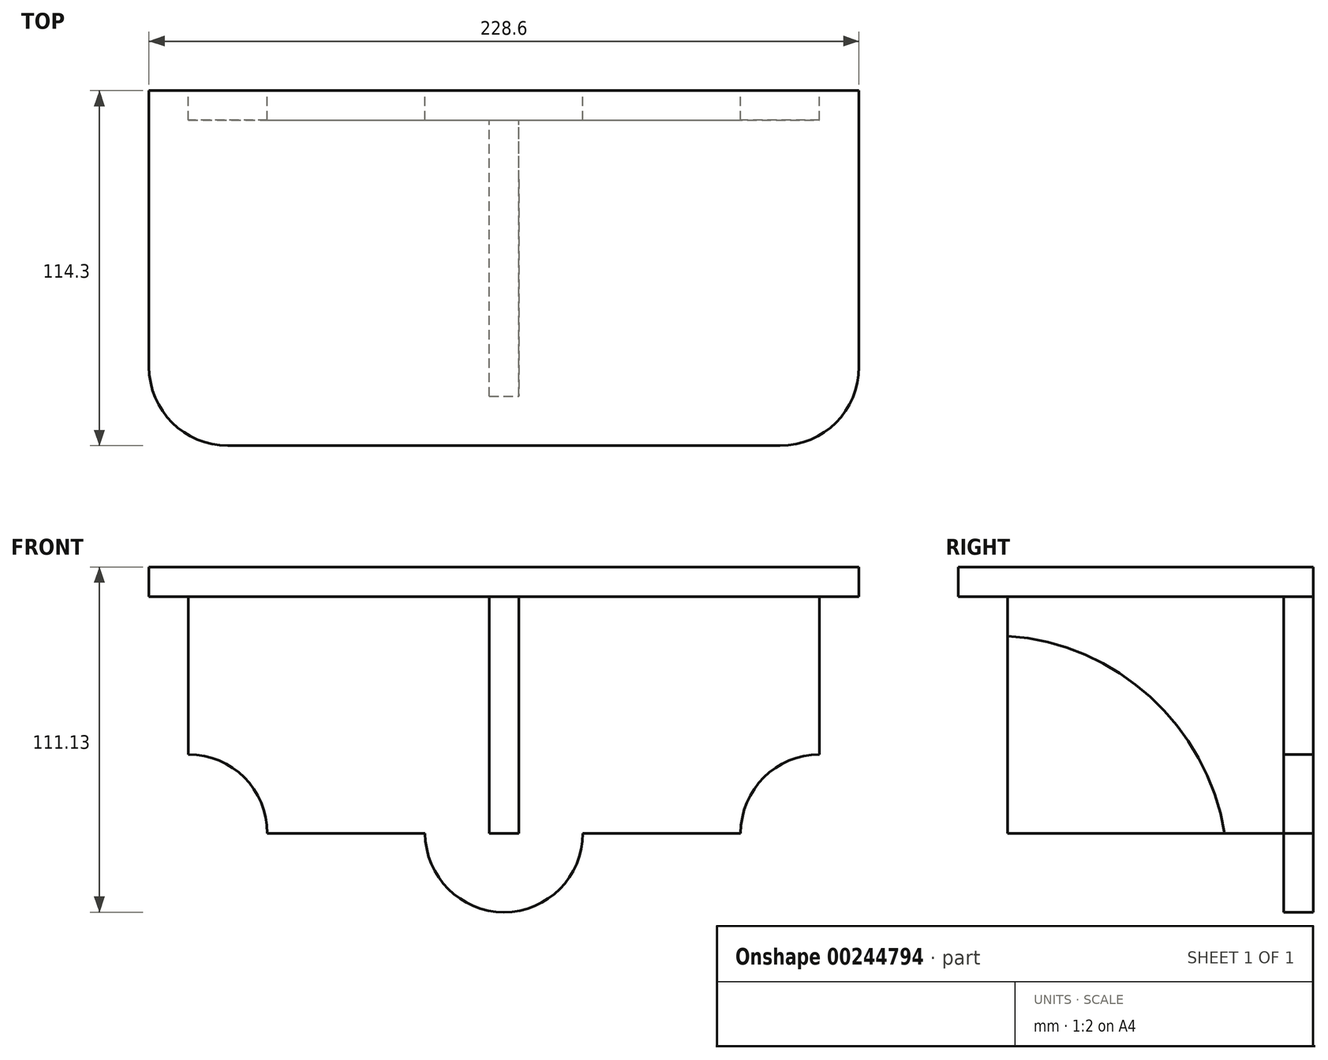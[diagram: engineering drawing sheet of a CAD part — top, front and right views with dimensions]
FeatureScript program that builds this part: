
annotation { "Feature Type Name" : "Feature", "Feature Type Description" : "" }
export const myFeature = defineFeature(function(context is Context, id is Id, definition is map)
    precondition{}
    {
        {
            var Q0;
            Q0=qCreatedBy(makeId("Front.planeOp"),FACE);
            var sketch = newSketch(context, id + "F0", { "sketchPlane" : qUnion([Q0])});
            skLineSegment(sketch, "E0", {"start": v(0, 0) * mm, "end": v(203.2, 0) * mm});
            skLineSegment(sketch, "E1", {"start": v(0, 0) * mm, "end": v(0, -50.8) * mm});
            skLineSegment(sketch, "E2", {"start": v(25.4, -76.2) * mm, "end": v(76.2, -76.2) * mm});
            skArc(sketch, "E3", {"start": v(0, -50.8) * mm, "mid": v(17.96, -58.24) * mm, "end": v(25.4, -76.2) * mm});
            skLineSegment(sketch, "E4", {"start": v(127, -76.2) * mm, "end": v(177.8, -76.2) * mm});
            skLineSegment(sketch, "E5", {"start": v(203.2, -50.8) * mm, "end": v(203.2, 0) * mm});
            skArc(sketch, "E6", {"start": v(127, -76.2) * mm, "mid": v(101.6, -101.6) * mm, "end": v(76.2, -76.2) * mm});
            skArc(sketch, "E7", {"start": v(203.2, -50.8) * mm, "mid": v(185.24, -58.24) * mm, "end": v(177.8, -76.2) * mm});
            skSolve(sketch);
        }
        {
            var Q0;
            Q0=makeQuery(id+"F0.imprint","IMPRINT",FACE,{"disambiguationData":[TD([[makeQuery(id+"F0.imprint","IMPRINT",EDGE,{"derivedFrom":sQuery(id+"F0.wireOp",EDGE,"E0")}),-1.0]])]});
            extrude(context, id + "F1", {"entities" : qUnion([Q0]), "depth" : 9.52 * mm});
        }
        {
            var Q0;
            Q0=makeQuery(id+"F1.opExtrude","CAP_FACE",FACE,{"disambiguationData":[OSD([sQuery(id+"F0.wireOp",EDGE,"E0"),sQuery(id+"F0.wireOp",EDGE,"E1"),sQuery(id+"F0.wireOp",EDGE,"E2"),sQuery(id+"F0.wireOp",EDGE,"E3"),sQuery(id+"F0.wireOp",EDGE,"E4"),sQuery(id+"F0.wireOp",EDGE,"E5"),sQuery(id+"F0.wireOp",EDGE,"E6"),sQuery(id+"F0.wireOp",EDGE,"E7")])],"isStart":false});
            var sketch = newSketch(context, id + "F2", { "sketchPlane" : qUnion([Q0])});
            skLineSegment(sketch, "E8", {"start": v(96.84, -76.2) * mm, "end": v(106.36, -76.2) * mm});
            skLineSegment(sketch, "E9", {"start": v(101.6, -76.2) * mm, "end": v(106.36, -76.2) * mm});
            skLineSegment(sketch, "E10", {"start": v(106.36, -76.2) * mm, "end": v(96.84, -76.2) * mm});
            skLineSegment(sketch, "E11", {"start": v(106.36, -76.2) * mm, "end": v(106.36, 0) * mm});
            skLineSegment(sketch, "E12", {"start": v(96.84, -76.2) * mm, "end": v(96.84, 0) * mm});
            skLineSegment(sketch, "E13", {"start": v(106.36, 0) * mm, "end": v(96.84, 0) * mm});
            skPoint(sketch, "E14.orphan", {"position": v(76.2, -76.2) * mm});
            skPoint(sketch, "E15.orphan", {"position": v(127, -76.2) * mm});
            skSolve(sketch);
        }
        {
            var Q0;
            {var subQ1=sQuery(id+"F2.wireOp",EDGE,"E11");Q0=makeQuery(id+"F2.imprint","IMPRINT",FACE,{"disambiguationData":[TD([[makeQuery(id+"F2.imprint","IMPRINT",EDGE,{"derivedFrom":subQ1}),1.0]])]});}
            extrude(context, id + "F3", {"entities" : qUnion([Q0]), "operationType" : NewBodyOperationType.ADD, "depth" : 88.9 * mm});
        }
        {
            var Q0;
            Q0=makeQuery(id+"F3.opExtrude","SWEPT_FACE",FACE,{"disambiguationData":[OSD([sQuery(id+"F2.wireOp",EDGE,"E11")])]});
            var sketch = newSketch(context, id + "F4", { "sketchPlane" : qUnion([Q0])});
            skLineSegment(sketch, "E16", {"start": v(-9.53, -76.2) * mm, "end": v(-28.57, -76.2) * mm});
            skLineSegment(sketch, "E17", {"start": v(-98.43, 0) * mm, "end": v(-98.43, -12.7) * mm});
            skArc(sketch, "E18", {"start": v(-28.57, -76.2) * mm, "mid": v(-52.48, -32.33) * mm, "end": v(-98.43, -12.7) * mm});
            skSolve(sketch);
        }
        {
            var Q0;
            {var subQ0=sQuery(id+"F4.wireOp",EDGE,"E18");Q0=makeQuery(id+"F4.imprint","IMPRINT",FACE,{"disambiguationData":[TD([[makeQuery(id+"F4.imprint","IMPRINT",EDGE,{"derivedFrom":subQ0}),1.0]])]});}
            extrude(context, id + "F5", {"entities" : qUnion([Q0]), "operationType" : NewBodyOperationType.REMOVE, "oppositeDirection" : true, "depth" : 3 / 203.2 * mm});
        }
        {
            var Q0;
            Q0=makeQuery(id+"F3.boolean.opBoolean","MERGE",FACE,{"derivedFrom":[makeQuery(id+"F1.opExtrude","SWEPT_FACE",FACE,{"disambiguationData":[OSD([sQuery(id+"F0.wireOp",EDGE,"E0")])]}),makeQuery(id+"F3.opExtrude","SWEPT_FACE",FACE,{"disambiguationData":[OSD([sQuery(id+"F2.wireOp",EDGE,"E13")])]})]});
            var sketch = newSketch(context, id + "F6", { "sketchPlane" : qUnion([Q0])});
            skLineSegment(sketch, "E19", {"start": v(0, 0) * mm, "end": v(-12.7, 0) * mm});
            skLineSegment(sketch, "E20", {"start": v(-12.7, 0) * mm, "end": v(-12.7, -88.9) * mm});
            skLineSegment(sketch, "E21", {"start": v(203.2, 0) * mm, "end": v(215.9, 0) * mm});
            skLineSegment(sketch, "E22", {"start": v(215.9, 0) * mm, "end": v(215.9, -88.9) * mm});
            skLineSegment(sketch, "E23", {"start": v(12.7, -114.3) * mm, "end": v(190.5, -114.3) * mm});
            skPoint(sketch, "E24.visualSharp", {"position": v(-12.7, -114.3) * mm});
            skArc(sketch, "E24.filletArc", {"start": v(-12.7, -88.9) * mm, "mid": v(-5.26, -106.86) * mm, "end": v(12.7, -114.3) * mm});
            skPoint(sketch, "E25.visualSharp", {"position": v(215.9, -114.3) * mm});
            skArc(sketch, "E25.filletArc", {"start": v(190.5, -114.3) * mm, "mid": v(208.46, -106.86) * mm, "end": v(215.9, -88.9) * mm});
            skSolve(sketch);
        }
        {
            var Q0;
            Q0=makeQuery(id+"F6.imprint","IMPRINT",FACE,{"disambiguationData":[TD([[makeQuery(id+"F6.imprint","IMPRINT",EDGE,{"derivedFrom":sQuery(id+"F6.wireOp",EDGE,"E19")}),1.0]])]});
            var Q1;
            {var subQ2=sQuery(id+"F0.wireOp",EDGE,"E0");Q1=makeQuery(id+"F6.imprint","IMPRINT",FACE,{"disambiguationData":[TD([[makeQuery(id+"F6.imprint","IMPRINT",EDGE,{"derivedFrom":makeQuery(id+"F1.opExtrude","CAP_EDGE",EDGE,{"disambiguationData":[OSD([subQ2])],"isStart":true})}),-1.0]])]});}
            extrude(context, id + "F7", {"entities" : qUnion([Q0, Q1]), "operationType" : NewBodyOperationType.ADD, "depth" : 9.52 * mm});
        }
    });
